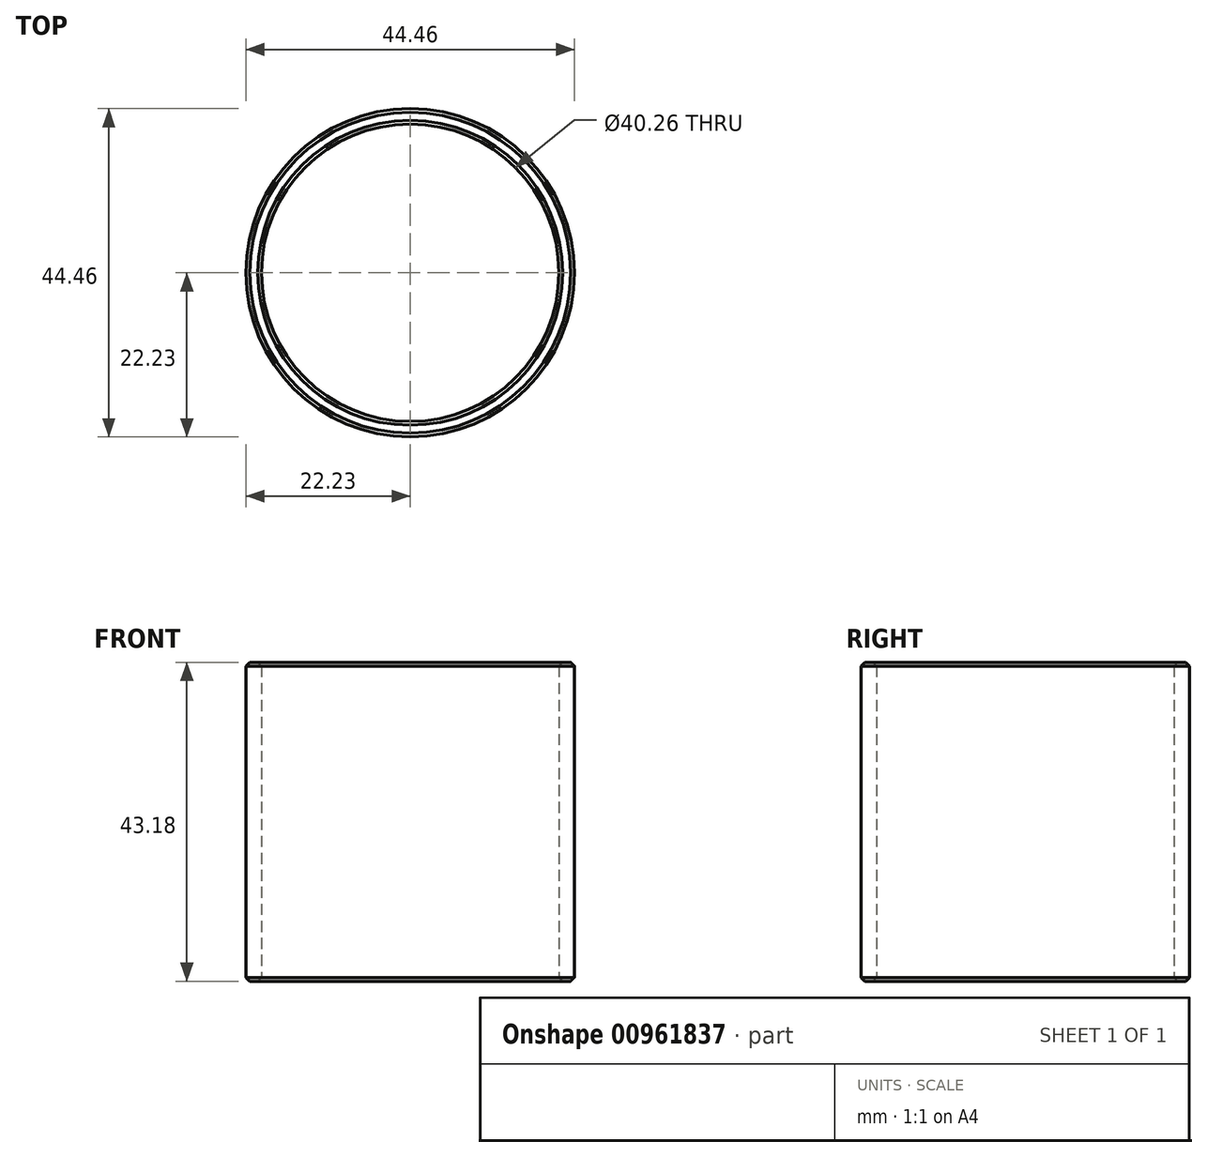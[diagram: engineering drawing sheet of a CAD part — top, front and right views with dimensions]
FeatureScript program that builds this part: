
annotation { "Feature Type Name" : "Feature", "Feature Type Description" : "" }
export const myFeature = defineFeature(function(context is Context, id is Id, definition is map)
    precondition{}
    {
        {
            var Q0;
            Q0=qCreatedBy(makeId("Top.planeOp"),FACE);
            var sketch = newSketch(context, id + "F0", { "sketchPlane" : qUnion([Q0])});
            skCircle(sketch, "E0", {"center": v(0, 0) * mm, "radius": 20.13 * mm});
            skCircle(sketch, "E1", {"center": v(0, 0) * mm, "radius": 22.23 * mm});
            skCircle(sketch, "E2", {"center": v(62.52, 47.5) * mm, "radius": 20.13 * mm});
            skCircle(sketch, "E3", {"center": v(62.52, 47.5) * mm, "radius": 22.23 * mm});
            skSolve(sketch);
        }
        {
            var Q0;
            Q0=makeQuery(id+"F0.imprint","IMPRINT",FACE,{"disambiguationData":[TD([[makeQuery(id+"F0.imprint","IMPRINT",EDGE,{"derivedFrom":sQuery(id+"F0.wireOp",EDGE,"E0")}),-1.0]])]});
            extrude(context, id + "F1", {"entities" : qUnion([Q0]), "depth" : 43.18 * mm, "offsetDistance" : 25.4 * mm});
        }
        {
            var Q0;
            Q0=makeQuery(id+"F1.opExtrude","CAP_EDGE",EDGE,{"disambiguationData":[OSD([sQuery(id+"F0.wireOp",EDGE,"E1")])],"isStart":false});
            var Q1;
            Q1=makeQuery(id+"F1.opExtrude","CAP_EDGE",EDGE,{"disambiguationData":[OSD([sQuery(id+"F0.wireOp",EDGE,"E0")])],"isStart":false});
            var Q2;
            Q2=makeQuery(id+"F1.opExtrude","CAP_EDGE",EDGE,{"disambiguationData":[OSD([sQuery(id+"F0.wireOp",EDGE,"E1")])],"isStart":true});
            var Q3;
            Q3=makeQuery(id+"F1.opExtrude","CAP_EDGE",EDGE,{"disambiguationData":[OSD([sQuery(id+"F0.wireOp",EDGE,"E0")])],"isStart":true});
            chamfer(context, id + "F2", {"entities" : qUnion([Q0, Q1, Q2, Q3]), "width" : 0.5 * mm, "tangentPropagation" : true});
        }
    });
